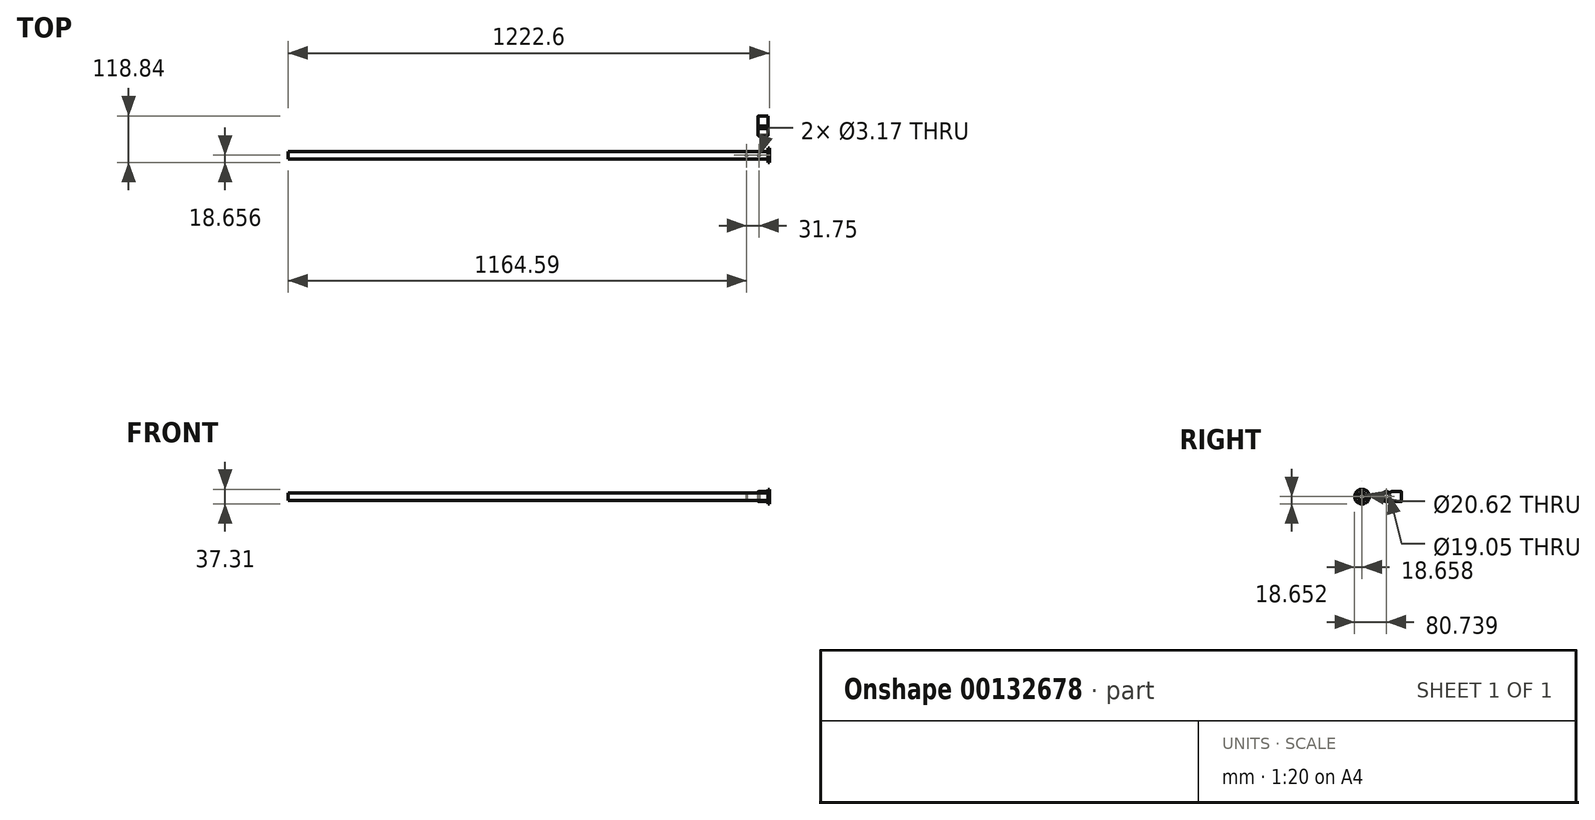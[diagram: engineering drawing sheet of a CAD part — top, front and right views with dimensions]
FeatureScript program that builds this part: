
annotation { "Feature Type Name" : "Feature", "Feature Type Description" : "" }
export const myFeature = defineFeature(function(context is Context, id is Id, definition is map)
    precondition{}
    {
        {
            var Q0;
            Q0=qCreatedBy(makeId("Right.planeOp"),FACE);
            var sketch = newSketch(context, id + "F0", { "sketchPlane" : qUnion([Q0])});
            skCircle(sketch, "E0", {"center": v(-68.64, 12.48) * mm, "radius": 9.53 * mm});
            skCircle(sketch, "E1", {"center": v(-6.56, 12.48) * mm, "radius": 9.53 * mm});
            skCircle(sketch, "E2", {"center": v(-6.56, 12.48) * mm, "radius": 12.7 * mm});
            skLineSegment(sketch, "E3.left", {"start": v(6.14, 25.18) * mm, "end": v(6.14, -0.22) * mm});
            skArc(sketch, "E4", {"start": v(-0.21, 23.48) * mm, "mid": v(3.2, 23.45) * mm, "end": v(6.14, 25.18) * mm});
            skArc(sketch, "E5", {"start": v(6.14, -0.22) * mm, "mid": v(3.2, 1.52) * mm, "end": v(-0.21, 1.48) * mm});
            skSolve(sketch);
        }
        {
            var Q0;
            Q0=makeQuery(id+"F0.imprint","IMPRINT",FACE,{"disambiguationData":[TD([[makeQuery(id+"F0.imprint","IMPRINT",EDGE,{"derivedFrom":sQuery(id+"F0.wireOp",EDGE,"E0")}),1.0]])]});
            extrude(context, id + "F1", {"entities" : qUnion([Q0]), "depth" : 25.4 * mm, "hasSecondDirection" : true, "secondDirectionOppositeDirection" : true, "secondDirectionDepth" : 1193.8 * mm});
        }
        {
            var Q0;
            Q0=qCreatedBy(makeId("Top.planeOp"),FACE);
            var sketch = newSketch(context, id + "F2", { "sketchPlane" : qUnion([Q0])});
            skPoint(sketch, "E6", {"position": v(2.54, -68.64) * mm});
            skPoint(sketch, "E7", {"position": v(-29.2, -68.64) * mm});
            skSolve(sketch);
        }
        {
            var Q0;
            Q0=sQuery(id+"F2.wireOp",VERTEX,"E7");
            var Q1;
            Q1=sQuery(id+"F2.wireOp",VERTEX,"E6");
            var Q2;
            Q2=makeQuery(id+"F1.opExtrude","SWEPT_BODY",BODY,{"disambiguationData":[OSD([sQuery(id+"F0.wireOp",EDGE,"E0")])]});
            hole(context, id + "F3", {"style" : HoleStyle.SIMPLE, "endStyle" : HoleEndStyle.THROUGH, "oppositeDirection" : true, "holeDiameter" : 3.17 * mm, "startFromSketch" : true, "locations" : qUnion([Q0, Q1]), "scope" : qUnion([Q2]), "isTappedThrough" : true});
        }
        {
            var Q0;
            Q0=makeQuery(id+"F1.opExtrude","CAP_FACE",FACE,{"disambiguationData":[OSD([sQuery(id+"F0.wireOp",EDGE,"E0")])],"isStart":false});
            var sketch = newSketch(context, id + "F4", { "sketchPlane" : qUnion([Q0])});
            skCircle(sketch, "E8", {"center": v(-68.64, 12.48) * mm, "radius": 10.31 * mm});
            skCircle(sketch, "E9", {"center": v(-68.64, 12.48) * mm, "radius": 18.66 * mm});
            skSolve(sketch);
        }
        {
            var Q0;
            Q0=makeQuery(id+"F4.imprint","IMPRINT",FACE,{"disambiguationData":[TD([[makeQuery(id+"F4.imprint","IMPRINT",EDGE,{"derivedFrom":sQuery(id+"F4.wireOp",EDGE,"E8")}),-1.0]])]});
            extrude(context, id + "F5", {"entities" : qUnion([Q0]), "depth" : 3.4 * mm});
        }
        {
            var Q0;
            Q0=makeQuery(id+"F0.imprint","IMPRINT",FACE,{"disambiguationData":[TD([[makeQuery(id+"F0.imprint","IMPRINT",EDGE,{"derivedFrom":sQuery(id+"F0.wireOp",EDGE,"E1")}),-1.0]])]});
            var Q1;
            {var subQ0=sQuery(id+"F0.wireOp",EDGE,"U7eqhkIY-EMrw-JvkB-tcnY-adYVxQQn6M5W");Q1=makeQuery(id+"F0.imprint","IMPRINT",FACE,{"disambiguationData":[TD([[makeQuery(id+"F0.imprint","IMPRINT",EDGE,{"derivedFrom":subQ0}),-1.0]])]});}
            var Q2;
            {var subQ3=sQuery(id+"F0.wireOp",EDGE,"E3.bottom");Q2=makeQuery(id+"F0.imprint","IMPRINT",FACE,{"disambiguationData":[TD([[makeQuery(id+"F0.imprint","IMPRINT",EDGE,{"derivedFrom":subQ3}),-1.0]])]});}
            var Q3;
            {var subQ0=sQuery(id+"F0.wireOp",EDGE,"E4");Q3=makeQuery(id+"F0.imprint","IMPRINT",FACE,{"disambiguationData":[TD([[makeQuery(id+"F0.imprint","IMPRINT",EDGE,{"derivedFrom":subQ0}),-1.0]])]});}
            var Q4;
            {var subQ0=sQuery(id+"F0.wireOp",EDGE,"E5");Q4=makeQuery(id+"F0.imprint","IMPRINT",FACE,{"disambiguationData":[TD([[makeQuery(id+"F0.imprint","IMPRINT",EDGE,{"derivedFrom":subQ0}),-1.0]])]});}
            extrude(context, id + "F6", {"entities" : qUnion([Q0, Q1, Q2, Q3, Q4]), "depth" : 25.4 * mm});
        }
        {
            var Q0;
            Q0=makeQuery(id+"F6.opExtrude","CAP_EDGE",EDGE,{"disambiguationData":[OSD([sQuery(id+"F0.wireOp",EDGE,"E1")])],"isStart":false});
            var Q1;
            Q1=makeQuery(id+"F6.opExtrude","CAP_EDGE",EDGE,{"disambiguationData":[OSD([sQuery(id+"F0.wireOp",EDGE,"E1")])],"isStart":true});
            fillet(context, id + "F7", {"entities" : qUnion([Q0, Q1]), "radius" : 0.5 * mm, "tangentPropagation" : true, "allowEdgeOverflow" : false});
        }
        {
            var Q0;
            Q0=makeQuery(id+"F6.opExtrude","CAP_EDGE",EDGE,{"disambiguationData":[OSD([sQuery(id+"F0.wireOp",EDGE,"E2")])],"isStart":false});
            var Q1;
            Q1=makeQuery(id+"F6.opExtrude","CAP_EDGE",EDGE,{"disambiguationData":[OSD([sQuery(id+"F0.wireOp",EDGE,"E4")])],"isStart":false});
            var Q2;
            Q2=makeQuery(id+"F6.opExtrude","CAP_EDGE",EDGE,{"disambiguationData":[OSD([sQuery(id+"F0.wireOp",EDGE,"E5")])],"isStart":false});
            var Q3;
            Q3=makeQuery(id+"F6.opExtrude","CAP_EDGE",EDGE,{"disambiguationData":[OSD([sQuery(id+"F0.wireOp",EDGE,"E2")])],"isStart":true});
            var Q4;
            Q4=makeQuery(id+"F6.opExtrude","CAP_EDGE",EDGE,{"disambiguationData":[OSD([sQuery(id+"F0.wireOp",EDGE,"E4")])],"isStart":true});
            var Q5;
            Q5=makeQuery(id+"F6.opExtrude","CAP_EDGE",EDGE,{"disambiguationData":[OSD([sQuery(id+"F0.wireOp",EDGE,"E5")])],"isStart":true});
            fillet(context, id + "F8", {"entities" : qUnion([Q0, Q1, Q2, Q3, Q4, Q5]), "radius" : 1.27 * mm, "tangentPropagation" : true, "allowEdgeOverflow" : false});
        }
        {
            var Q0;
            Q0=makeQuery(id+"F6.opExtrude","SWEPT_FACE",FACE,{"disambiguationData":[OSD([sQuery(id+"F0.wireOp",EDGE,"E3.left")])]});
            var sketch = newSketch(context, id + "F9", { "sketchPlane" : qUnion([Q0])});
            skLineSegment(sketch, "E10.bottom", {"start": v(-25.4, 25.18) * mm, "end": v(0, 25.18) * mm});
            skLineSegment(sketch, "E10.top", {"start": v(-25.4, -0.22) * mm, "end": v(0, -0.22) * mm});
            skLineSegment(sketch, "E10.left", {"start": v(-25.4, 25.18) * mm, "end": v(-25.4, -0.22) * mm});
            skLineSegment(sketch, "E10.right", {"start": v(0, 25.18) * mm, "end": v(0, -0.22) * mm});
            skSolve(sketch);
        }
        {
            var Q0;
            {var subQ1=makeQuery(id+"F6.opExtrude","SWEPT_FACE",FACE,{"disambiguationData":[OSD([sQuery(id+"F0.wireOp",EDGE,"E3.left")])]});var subQ2=sQuery(id+"F0.wireOp",EDGE,"E4");var subQ3=makeQuery(id+"F8.opFillet","BLEND_EDGE",EDGE,{"blendedFrom":[makeQuery(id+"F6.opExtrude","CAP_EDGE",EDGE,{"disambiguationData":[OSD([subQ2])],"isStart":true}),subQ1],"blendedInto":[subQ1]});Q0=makeQuery(id+"F9.imprint","IMPRINT",FACE,{"disambiguationData":[TD([[makeQuery(id+"F9.imprint","IMPRINT",EDGE,{"derivedFrom":subQ3}),1.0]])]});}
            extrude(context, id + "F10", {"entities" : qUnion([Q0]), "operationType" : NewBodyOperationType.ADD, "depth" : 25.4 * mm});
        }
    });
